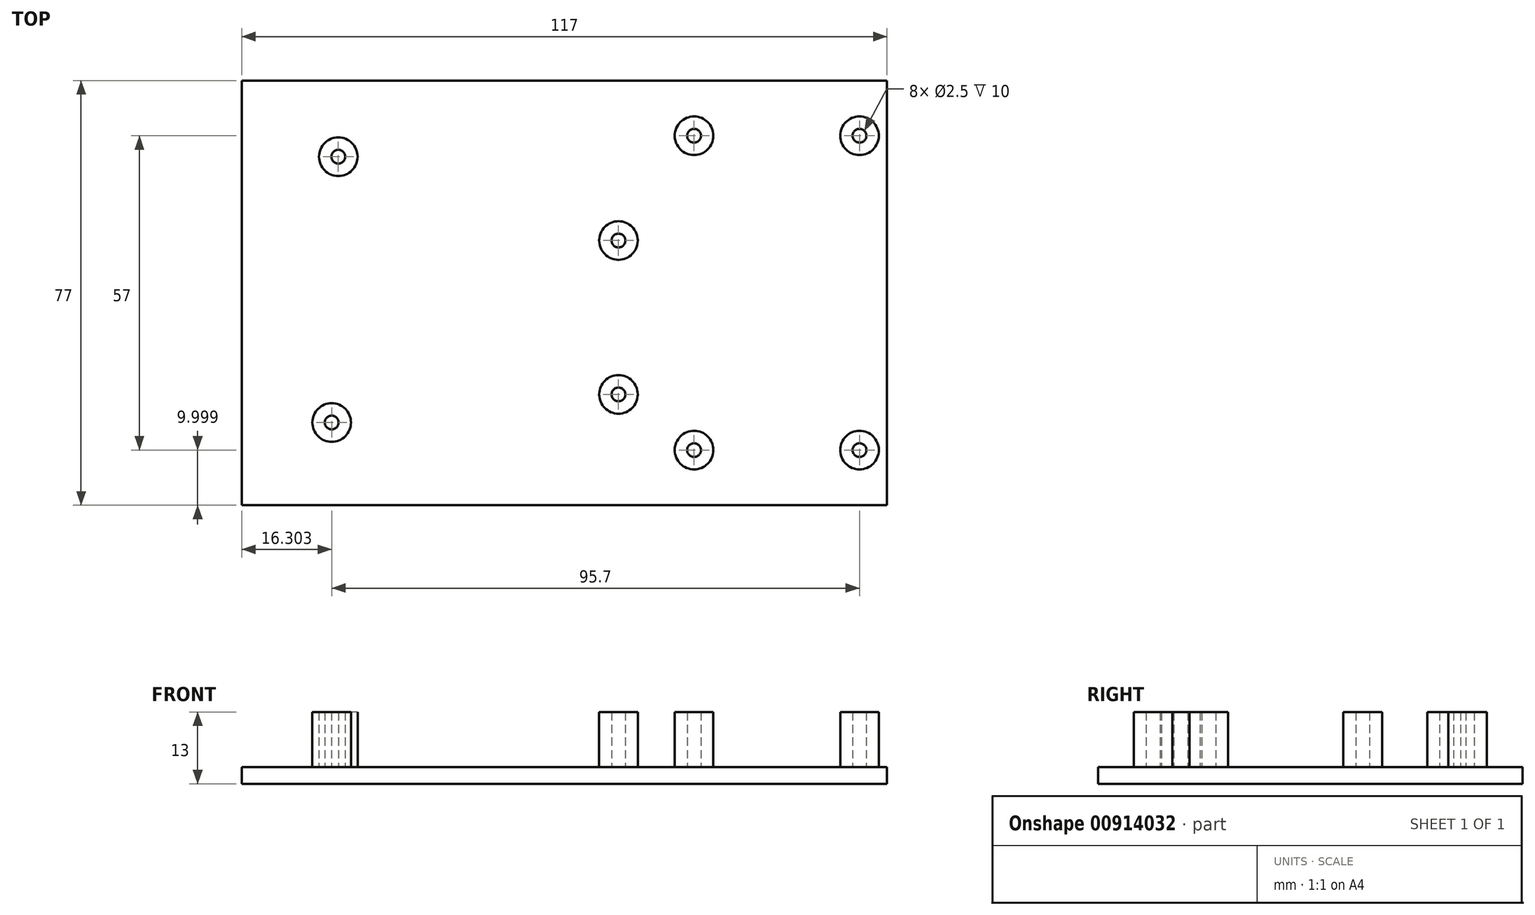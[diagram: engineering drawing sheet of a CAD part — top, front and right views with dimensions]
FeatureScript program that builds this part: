
annotation { "Feature Type Name" : "Feature", "Feature Type Description" : "" }
export const myFeature = defineFeature(function(context is Context, id is Id, definition is map)
    precondition{}
    {
        {
            var Q0;
            Q0=qCreatedBy(makeId("Top.planeOp"),FACE);
            var sketch = newSketch(context, id + "F0", { "sketchPlane" : qUnion([Q0])});
            skLineSegment(sketch, "E0.bottom", {"start": v(-57.22, 37.3) * mm, "end": v(59.78, 37.3) * mm});
            skLineSegment(sketch, "E0.top", {"start": v(-57.22, -39.7) * mm, "end": v(59.78, -39.7) * mm});
            skLineSegment(sketch, "E0.left", {"start": v(-57.22, 37.3) * mm, "end": v(-57.22, -39.7) * mm});
            skLineSegment(sketch, "E0.right", {"start": v(59.78, 37.3) * mm, "end": v(59.78, -39.7) * mm});
            skCircle(sketch, "E1", {"center": v(-39.72, 23.5) * mm, "radius": 1.25 * mm});
            skCircle(sketch, "E2", {"center": v(11.08, 8.3) * mm, "radius": 1.25 * mm});
            skCircle(sketch, "E3", {"center": v(11.08, -19.6) * mm, "radius": 1.25 * mm});
            skCircle(sketch, "E4", {"center": v(-40.92, -24.7) * mm, "radius": 1.25 * mm});
            skLineSegment(sketch, "E5", {"start": v(11.08, 8.3) * mm, "end": v(11.08, -19.6) * mm, "construction": true});
            skCircle(sketch, "E6", {"center": v(-39.72, 23.5) * mm, "radius": 3.5 * mm});
            skCircle(sketch, "E7", {"center": v(11.08, 8.3) * mm, "radius": 3.5 * mm});
            skCircle(sketch, "E8", {"center": v(11.08, -19.6) * mm, "radius": 3.5 * mm});
            skCircle(sketch, "E9", {"center": v(-40.92, -24.7) * mm, "radius": 3.5 * mm});
            skCircle(sketch, "E10", {"center": v(24.78, 27.3) * mm, "radius": 3.5 * mm});
            skCircle(sketch, "E11", {"center": v(24.78, 27.3) * mm, "radius": 1.25 * mm});
            skCircle(sketch, "E12", {"center": v(54.78, 27.3) * mm, "radius": 3.5 * mm});
            skCircle(sketch, "E13", {"center": v(54.78, 27.3) * mm, "radius": 1.25 * mm});
            skCircle(sketch, "E14", {"center": v(54.78, -29.7) * mm, "radius": 3.5 * mm});
            skCircle(sketch, "E15", {"center": v(54.78, -29.7) * mm, "radius": 1.25 * mm});
            skCircle(sketch, "E16", {"center": v(24.78, -29.7) * mm, "radius": 3.5 * mm});
            skCircle(sketch, "E17", {"center": v(24.78, -29.7) * mm, "radius": 1.25 * mm});
            skSolve(sketch);
        }
        {
            var Q0;
            Q0=makeQuery(id+"F0.imprint","IMPRINT",FACE,{"disambiguationData":[TD([[makeQuery(id+"F0.imprint","IMPRINT",EDGE,{"derivedFrom":sQuery(id+"F0.wireOp",EDGE,"E0.bottom")}),-1.0]])]});
            var Q1;
            Q1=makeQuery(id+"F0.imprint","IMPRINT",FACE,{"disambiguationData":[TD([[makeQuery(id+"F0.imprint","IMPRINT",EDGE,{"derivedFrom":sQuery(id+"F0.wireOp",EDGE,"E1")}),-1.0]])]});
            var Q2;
            Q2=makeQuery(id+"F0.imprint","IMPRINT",FACE,{"disambiguationData":[TD([[makeQuery(id+"F0.imprint","IMPRINT",EDGE,{"derivedFrom":sQuery(id+"F0.wireOp",EDGE,"E2")}),1.0]])]});
            var Q3;
            Q3=makeQuery(id+"F0.imprint","IMPRINT",FACE,{"disambiguationData":[TD([[makeQuery(id+"F0.imprint","IMPRINT",EDGE,{"derivedFrom":sQuery(id+"F0.wireOp",EDGE,"E2")}),-1.0]])]});
            var Q4;
            Q4=makeQuery(id+"F0.imprint","IMPRINT",FACE,{"disambiguationData":[TD([[makeQuery(id+"F0.imprint","IMPRINT",EDGE,{"derivedFrom":sQuery(id+"F0.wireOp",EDGE,"E3")}),1.0]])]});
            var Q5;
            Q5=makeQuery(id+"F0.imprint","IMPRINT",FACE,{"disambiguationData":[TD([[makeQuery(id+"F0.imprint","IMPRINT",EDGE,{"derivedFrom":sQuery(id+"F0.wireOp",EDGE,"E3")}),-1.0]])]});
            var Q6;
            Q6=makeQuery(id+"F0.imprint","IMPRINT",FACE,{"disambiguationData":[TD([[makeQuery(id+"F0.imprint","IMPRINT",EDGE,{"derivedFrom":sQuery(id+"F0.wireOp",EDGE,"E4")}),1.0]])]});
            var Q7;
            Q7=makeQuery(id+"F0.imprint","IMPRINT",FACE,{"disambiguationData":[TD([[makeQuery(id+"F0.imprint","IMPRINT",EDGE,{"derivedFrom":sQuery(id+"F0.wireOp",EDGE,"E4")}),-1.0]])]});
            var Q8;
            Q8=makeQuery(id+"F0.imprint","IMPRINT",FACE,{"disambiguationData":[TD([[makeQuery(id+"F0.imprint","IMPRINT",EDGE,{"derivedFrom":sQuery(id+"F0.wireOp",EDGE,"E1")}),1.0]])]});
            var Q9;
            Q9=makeQuery(id+"F0.imprint","IMPRINT",FACE,{"disambiguationData":[TD([[makeQuery(id+"F0.imprint","IMPRINT",EDGE,{"derivedFrom":sQuery(id+"F0.wireOp",EDGE,"E10")}),1.0]])]});
            var Q10;
            Q10=makeQuery(id+"F0.imprint","IMPRINT",FACE,{"disambiguationData":[TD([[makeQuery(id+"F0.imprint","IMPRINT",EDGE,{"derivedFrom":sQuery(id+"F0.wireOp",EDGE,"E11")}),1.0]])]});
            var Q11;
            Q11=makeQuery(id+"F0.imprint","IMPRINT",FACE,{"disambiguationData":[TD([[makeQuery(id+"F0.imprint","IMPRINT",EDGE,{"derivedFrom":sQuery(id+"F0.wireOp",EDGE,"E13")}),1.0]])]});
            var Q12;
            Q12=makeQuery(id+"F0.imprint","IMPRINT",FACE,{"disambiguationData":[TD([[makeQuery(id+"F0.imprint","IMPRINT",EDGE,{"derivedFrom":sQuery(id+"F0.wireOp",EDGE,"E12")}),1.0]])]});
            var Q13;
            Q13=makeQuery(id+"F0.imprint","IMPRINT",FACE,{"disambiguationData":[TD([[makeQuery(id+"F0.imprint","IMPRINT",EDGE,{"derivedFrom":sQuery(id+"F0.wireOp",EDGE,"E15")}),1.0]])]});
            var Q14;
            Q14=makeQuery(id+"F0.imprint","IMPRINT",FACE,{"disambiguationData":[TD([[makeQuery(id+"F0.imprint","IMPRINT",EDGE,{"derivedFrom":sQuery(id+"F0.wireOp",EDGE,"E14")}),1.0]])]});
            var Q15;
            Q15=makeQuery(id+"F0.imprint","IMPRINT",FACE,{"disambiguationData":[TD([[makeQuery(id+"F0.imprint","IMPRINT",EDGE,{"derivedFrom":sQuery(id+"F0.wireOp",EDGE,"E17")}),1.0]])]});
            var Q16;
            Q16=makeQuery(id+"F0.imprint","IMPRINT",FACE,{"disambiguationData":[TD([[makeQuery(id+"F0.imprint","IMPRINT",EDGE,{"derivedFrom":sQuery(id+"F0.wireOp",EDGE,"E16")}),1.0]])]});
            extrude(context, id + "F1", {"entities" : qUnion([Q0, Q1, Q2, Q3, Q4, Q5, Q6, Q7, Q8, Q9, Q10, Q11, Q12, Q13, Q14, Q15, Q16]), "oppositeDirection" : true, "depth" : 3 * mm, "offsetDistance" : 25 * mm});
        }
        {
            var Q0;
            Q0=makeQuery(id+"F0.imprint","IMPRINT",FACE,{"disambiguationData":[TD([[makeQuery(id+"F0.imprint","IMPRINT",EDGE,{"derivedFrom":sQuery(id+"F0.wireOp",EDGE,"E1")}),-1.0]])]});
            var Q1;
            Q1=makeQuery(id+"F0.imprint","IMPRINT",FACE,{"disambiguationData":[TD([[makeQuery(id+"F0.imprint","IMPRINT",EDGE,{"derivedFrom":sQuery(id+"F0.wireOp",EDGE,"E2")}),-1.0]])]});
            var Q2;
            Q2=makeQuery(id+"F0.imprint","IMPRINT",FACE,{"disambiguationData":[TD([[makeQuery(id+"F0.imprint","IMPRINT",EDGE,{"derivedFrom":sQuery(id+"F0.wireOp",EDGE,"E3")}),-1.0]])]});
            var Q3;
            Q3=makeQuery(id+"F0.imprint","IMPRINT",FACE,{"disambiguationData":[TD([[makeQuery(id+"F0.imprint","IMPRINT",EDGE,{"derivedFrom":sQuery(id+"F0.wireOp",EDGE,"E4")}),-1.0]])]});
            var Q4;
            Q4=makeQuery(id+"F0.imprint","IMPRINT",FACE,{"disambiguationData":[TD([[makeQuery(id+"F0.imprint","IMPRINT",EDGE,{"derivedFrom":sQuery(id+"F0.wireOp",EDGE,"E16")}),1.0]])]});
            var Q5;
            Q5=makeQuery(id+"F0.imprint","IMPRINT",FACE,{"disambiguationData":[TD([[makeQuery(id+"F0.imprint","IMPRINT",EDGE,{"derivedFrom":sQuery(id+"F0.wireOp",EDGE,"E14")}),1.0]])]});
            var Q6;
            Q6=makeQuery(id+"F0.imprint","IMPRINT",FACE,{"disambiguationData":[TD([[makeQuery(id+"F0.imprint","IMPRINT",EDGE,{"derivedFrom":sQuery(id+"F0.wireOp",EDGE,"E10")}),1.0]])]});
            var Q7;
            Q7=makeQuery(id+"F0.imprint","IMPRINT",FACE,{"disambiguationData":[TD([[makeQuery(id+"F0.imprint","IMPRINT",EDGE,{"derivedFrom":sQuery(id+"F0.wireOp",EDGE,"E12")}),1.0]])]});
            extrude(context, id + "F2", {"entities" : qUnion([Q0, Q1, Q2, Q3, Q4, Q5, Q6, Q7]), "operationType" : NewBodyOperationType.ADD, "depth" : 10 * mm, "offsetDistance" : 25 * mm});
        }
    });
